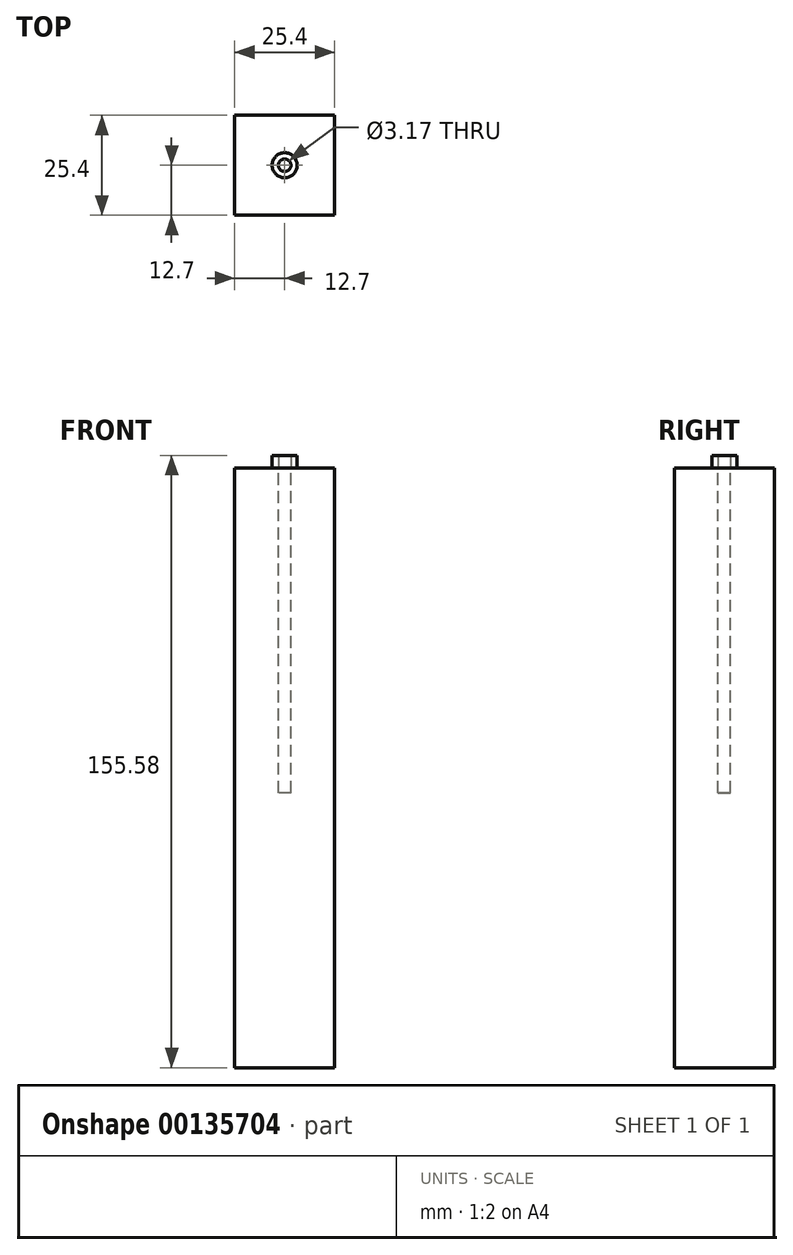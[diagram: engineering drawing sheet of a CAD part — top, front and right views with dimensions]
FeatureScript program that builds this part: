
annotation { "Feature Type Name" : "Feature", "Feature Type Description" : "" }
export const myFeature = defineFeature(function(context is Context, id is Id, definition is map)
    precondition{}
    {
        {
            var Q0;
            Q0=qCreatedBy(makeId("Top.planeOp"),FACE);
            var sketch = newSketch(context, id + "F0", { "sketchPlane" : qUnion([Q0])});
            skCircle(sketch, "E0", {"center": v(0, 0) * mm, "radius": 1.59 * mm});
            skSolve(sketch);
        }
        {
            var Q0;
            Q0 = qSketchRegion(id + "F0", true);
            extrude(context, id + "F1", {"entities" : qUnion([Q0]), "oppositeDirection" : true, "depth" : 82.55 * mm});
        }
        {
            var Q0;
            Q0=qCreatedBy(makeId("Top.planeOp"),FACE);
            var sketch = newSketch(context, id + "F2", { "sketchPlane" : qUnion([Q0])});
            skCircle(sketch, "E1", {"center": v(0, 0) * mm, "radius": 1.59 * mm});
            skCircle(sketch, "E2", {"center": v(0, 0) * mm, "radius": 3.18 * mm});
            skSolve(sketch);
        }
        {
            var Q0;
            Q0 = qSketchRegion(id + "F2", true);
            extrude(context, id + "F3", {"entities" : qUnion([Q0]), "depth" : 3.17 * mm});
        }
        {
            var Q0;
            Q0=qCreatedBy(makeId("Top.planeOp"),FACE);
            var sketch = newSketch(context, id + "F4", { "sketchPlane" : qUnion([Q0])});
            skLineSegment(sketch, "E3.bottom", {"start": v(-12.7, -12.7) * mm, "end": v(12.7, -12.7) * mm});
            skLineSegment(sketch, "E3.top", {"start": v(-12.7, 12.7) * mm, "end": v(12.7, 12.7) * mm});
            skLineSegment(sketch, "E3.left", {"start": v(-12.7, -12.7) * mm, "end": v(-12.7, 12.7) * mm});
            skLineSegment(sketch, "E3.right", {"start": v(12.7, -12.7) * mm, "end": v(12.7, 12.7) * mm});
            skPoint(sketch, "E3.middle", {"position": v(0, 0) * mm});
            skSolve(sketch);
        }
        {
            var Q0;
            Q0=makeQuery(id+"F4.imprint","IMPRINT",FACE,{"disambiguationData":[TD([[makeQuery(id+"F4.imprint","IMPRINT",EDGE,{"derivedFrom":sQuery(id+"F4.wireOp",EDGE,"E3.bottom")}),1.0]])]});
            extrude(context, id + "F5", {"entities" : qUnion([Q0]), "oppositeDirection" : true, "depth" : 152.4 * mm});
        }
    });
